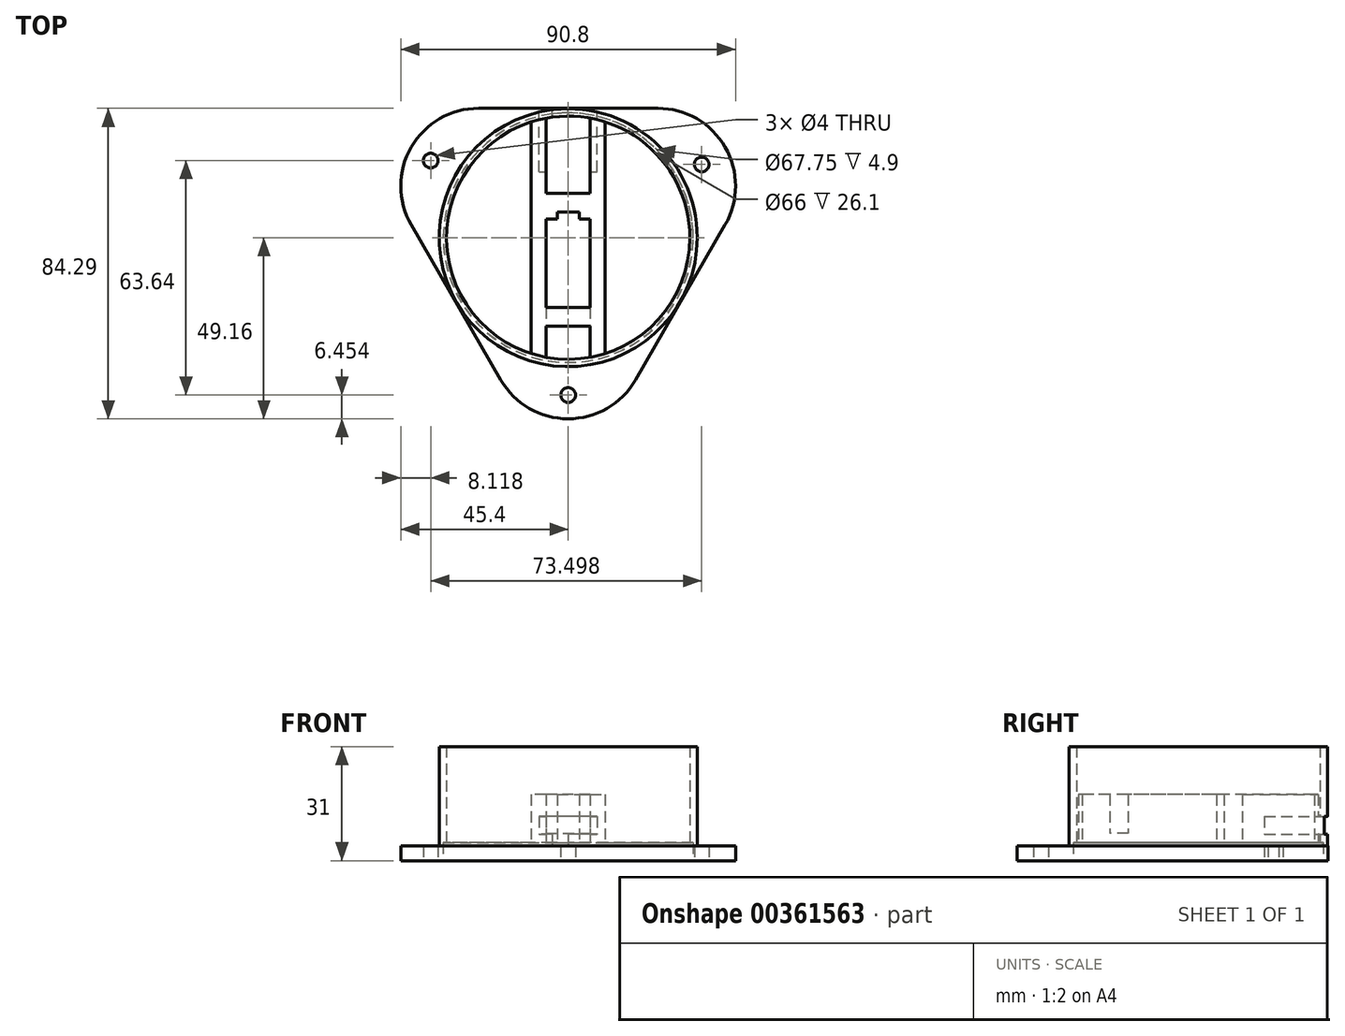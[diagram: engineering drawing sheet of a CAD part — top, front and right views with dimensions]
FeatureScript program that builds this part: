
annotation { "Feature Type Name" : "Feature", "Feature Type Description" : "" }
export const myFeature = defineFeature(function(context is Context, id is Id, definition is map)
    precondition{}
    {
        {
            var Q0;
            Q0=qCreatedBy(makeId("Top.planeOp"),FACE);
            var sketch = newSketch(context, id + "F0", { "sketchPlane" : qUnion([Q0])});
            skCircle(sketch, "E0", {"center": v(0, 0) * mm, "radius": 35 * mm});
            skCircle(sketch, "E1", {"center": v(0, 0) * mm, "radius": 33 * mm});
            skSolve(sketch);
        }
        {
            var Q0;
            Q0=qCreatedBy(makeId("Top.planeOp"),FACE);
            var sketch = newSketch(context, id + "F1", { "sketchPlane" : qUnion([Q0])});
            skPoint(sketch, "E2", {"position": v(0, -24) * mm});
            skPoint(sketch, "E3", {"position": v(0, -19) * mm});
            skPoint(sketch, "E4", {"position": v(6, -19) * mm});
            skPoint(sketch, "E5", {"position": v(-6, -19) * mm});
            skPoint(sketch, "E6", {"position": v(6, -24) * mm});
            skPoint(sketch, "E7", {"position": v(-6, -24) * mm});
            skPoint(sketch, "E8", {"position": v(10, -24) * mm});
            skLineSegment(sketch, "E9", {"start": v(10, -24) * mm, "end": v(10, -32.05) * mm});
            skLineSegment(sketch, "E10", {"start": v(6, -24) * mm, "end": v(6, -33.1) * mm});
            skPoint(sketch, "E11", {"position": v(6, 5) * mm});
            skPoint(sketch, "E12", {"position": v(3, 5) * mm});
            skPoint(sketch, "E13", {"position": v(3, 7) * mm});
            skPoint(sketch, "E14", {"position": v(3, 12) * mm});
            skPoint(sketch, "E15", {"position": v(6, 12) * mm});
            skPoint(sketch, "E16", {"position": v(10, 5) * mm});
            skPoint(sketch, "E17", {"position": v(10, 12) * mm});
            skLineSegment(sketch, "E18", {"start": v(10, -24) * mm, "end": v(10, 32.28) * mm});
            skLineSegment(sketch, "E19", {"start": v(6, 12) * mm, "end": v(6, 33.47) * mm});
            skLineSegment(sketch, "E20", {"start": v(6, 12) * mm, "end": v(3, 12) * mm});
            skLineSegment(sketch, "E21", {"start": v(3, 7) * mm, "end": v(3, 5) * mm});
            skLineSegment(sketch, "E22", {"start": v(3, 5) * mm, "end": v(6, 5) * mm});
            skLineSegment(sketch, "E23", {"start": v(6, 5) * mm, "end": v(6, -19) * mm});
            skPoint(sketch, "E24", {"position": v(0, 7) * mm});
            skPoint(sketch, "E25", {"position": v(0, 12) * mm});
            skLineSegment(sketch, "E26", {"start": v(3, 7) * mm, "end": v(0, 7) * mm});
            skLineSegment(sketch, "E27", {"start": v(3, 12) * mm, "end": v(0, 12) * mm});
            skLineSegment(sketch, "E28", {"start": v(0, -24) * mm, "end": v(6, -24) * mm});
            skLineSegment(sketch, "E29", {"start": v(0, -19) * mm, "end": v(6, -19) * mm});
            skLineSegment(sketch, "E30.MirrorCS", {"start": v(-3, 12) * mm, "end": v(0, 12) * mm});
            skLineSegment(sketch, "E31.MirrorCS", {"start": v(-6, 12) * mm, "end": v(-3, 12) * mm});
            skLineSegment(sketch, "E32.MirrorCS", {"start": v(-6, 12) * mm, "end": v(-6, 33.47) * mm});
            skLineSegment(sketch, "E33.MirrorCS", {"start": v(-10, -24) * mm, "end": v(-10, 32.28) * mm});
            skLineSegment(sketch, "E34.MirrorCS", {"start": v(-6, 5) * mm, "end": v(-6, -19) * mm});
            skLineSegment(sketch, "E35.MirrorCS", {"start": v(-3, 5) * mm, "end": v(-6, 5) * mm});
            skLineSegment(sketch, "E36.MirrorCS", {"start": v(-3, 7) * mm, "end": v(-3, 5) * mm});
            skLineSegment(sketch, "E37.MirrorCS", {"start": v(-3, 7) * mm, "end": v(0, 7) * mm});
            skLineSegment(sketch, "E38.MirrorCS", {"start": v(0, -19) * mm, "end": v(-6, -19) * mm});
            skLineSegment(sketch, "E39.MirrorCS", {"start": v(0, -24) * mm, "end": v(-6, -24) * mm});
            skLineSegment(sketch, "E40.MirrorCS", {"start": v(-6, -24) * mm, "end": v(-6, -33.1) * mm});
            skLineSegment(sketch, "E41.MirrorCS", {"start": v(-10, -24) * mm, "end": v(-10, -32.05) * mm});
            skLineSegment(sketch, "E42", {"start": v(6, 33.47) * mm, "end": v(10, 32.28) * mm});
            skLineSegment(sketch, "E43", {"start": v(-6, 33.47) * mm, "end": v(-10, 32.28) * mm});
            skLineSegment(sketch, "E44", {"start": v(-10, -32.05) * mm, "end": v(-6, -33.1) * mm});
            skLineSegment(sketch, "E45", {"start": v(6, -33.1) * mm, "end": v(10, -32.05) * mm});
            skSolve(sketch);
        }
        {
            var Q0;
            Q0=makeQuery(id+"F0.imprint","IMPRINT",FACE,{"disambiguationData":[TD([[makeQuery(id+"F0.imprint","IMPRINT",EDGE,{"derivedFrom":sQuery(id+"F0.wireOp",EDGE,"E0")}),1.0]])]});
            extrude(context, id + "F2", {"entities" : qUnion([Q0]), "depth" : 31 * mm});
        }
        {
            var Q0;
            Q0=makeQuery(id+"F1.imprint","IMPRINT",FACE,{"disambiguationData":[TD([[makeQuery(id+"F1.imprint","IMPRINT",EDGE,{"derivedFrom":sQuery(id+"F1.wireOp",EDGE,"E9")}),-1.0]])]});
            extrude(context, id + "F3", {"entities" : qUnion([Q0]), "operationType" : NewBodyOperationType.ADD, "depth" : 18 * mm});
        }
        {
            var Q0;
            Q0=sQuery(id+"F1.wireOp",EDGE,"E28");
            var Q1;
            Q1=sQuery(id+"F1.wireOp",EDGE,"E39.MirrorCS");
            extrude(context, id + "F4", {"bodyType" : ToolBodyType.SURFACE, "surfaceEntities" : qUnion([Q0, Q1]), "depth" : 7.5 * mm});
        }
        {
            var Q0;
            Q0=makeQuery(id+"F4.opExtrude","SWEPT_FACE",FACE,{"disambiguationData":[OSD([sQuery(id+"F1.wireOp",EDGE,"E28"),sQuery(id+"F1.wireOp",EDGE,"E39.MirrorCS")])]});
            extrude(context, id + "F5", {"entities" : qUnion([Q0]), "operationType" : NewBodyOperationType.REMOVE, "oppositeDirection" : true, "depth" : 9.3 * mm});
        }
        {
            var Q0;
            Q0=qCreatedBy(makeId("Top.planeOp"),FACE);
            var sketch = newSketch(context, id + "F6", { "sketchPlane" : qUnion([Q0])});
            skCircle(sketch, "E46.cCircle", {"center": v(0, 0) * mm, "radius": 35.13 * mm, "construction": true});
            skLineSegment(sketch, "E46.0", {"start": v(-60.85, 35.13) * mm, "end": v(60.85, 35.13) * mm});
            skLineSegment(sketch, "E46.1", {"start": v(60.85, 35.13) * mm, "end": v(0, -70.26) * mm});
            skLineSegment(sketch, "E46.2", {"start": v(0, -70.26) * mm, "end": v(-60.85, 35.13) * mm});
            skPoint(sketch, "E46.0.midPoint", {"position": v(0, 35.13) * mm});
            skSolve(sketch);
        }
        {
            var Q0;
            Q0=makeQuery(id+"F6.imprint","IMPRINT",FACE,{"disambiguationData":[TD([[makeQuery(id+"F6.imprint","IMPRINT",EDGE,{"derivedFrom":sQuery(id+"F6.wireOp",EDGE,"E46.0")}),-1.0]])]});
            extrude(context, id + "F7", {"entities" : qUnion([Q0]), "operationType" : NewBodyOperationType.ADD, "depth" : 4 * mm});
        }
        {
            var Q0;
            Q0=makeQuery(id+"F7.opExtrude","SWEPT_EDGE",EDGE,{"disambiguationData":[OSD([sQuery(id+"F6.wireOp",EDGE,"E46.0"),sQuery(id+"F6.wireOp",EDGE,"E46.2")])]});
            var Q1;
            Q1=makeQuery(id+"F7.opExtrude","SWEPT_EDGE",EDGE,{"disambiguationData":[OSD([sQuery(id+"F6.wireOp",EDGE,"E46.0"),sQuery(id+"F6.wireOp",EDGE,"E46.1")])]});
            var Q2;
            Q2=makeQuery(id+"F7.opExtrude","SWEPT_EDGE",EDGE,{"disambiguationData":[OSD([sQuery(id+"F6.wireOp",EDGE,"E46.1"),sQuery(id+"F6.wireOp",EDGE,"E46.2")])]});
            fillet(context, id + "F8", {"entities" : qUnion([Q0, Q1, Q2]), "radius" : 21.1 * mm, "tangentPropagation" : true, "allowEdgeOverflow" : false});
        }
        {
            var Q0;
            Q0=qCreatedBy(makeId("Top.planeOp"),FACE);
            var sketch = newSketch(context, id + "F9", { "sketchPlane" : qUnion([Q0])});
            skCircle(sketch, "E47", {"center": v(-37.28, 20.93) * mm, "radius": 2 * mm});
            skCircle(sketch, "E48", {"center": v(0, -42.7) * mm, "radius": 2 * mm});
            skCircle(sketch, "E49", {"center": v(36.22, 19.89) * mm, "radius": 2 * mm});
            skSolve(sketch);
        }
        {
            var Q0;
            Q0 = qSketchRegion(id + "F9", true);
            extrude(context, id + "F10", {"entities" : qUnion([Q0]), "operationType" : NewBodyOperationType.REMOVE, "oppositeDirection" : true, "depth" : 38 * mm});
        }
        {
            var Q0;
            Q0=makeQuery(id+"F9.imprint","IMPRINT",FACE,{"disambiguationData":[TD([[makeQuery(id+"F9.imprint","IMPRINT",EDGE,{"derivedFrom":sQuery(id+"F9.wireOp",EDGE,"E49")}),1.0]])]});
            extrude(context, id + "F11", {"entities" : qUnion([Q0]), "operationType" : NewBodyOperationType.REMOVE, "depth" : 52 * mm});
        }
        {
            var Q0;
            Q0=makeQuery(id+"F9.imprint","IMPRINT",FACE,{"disambiguationData":[TD([[makeQuery(id+"F9.imprint","IMPRINT",EDGE,{"derivedFrom":sQuery(id+"F9.wireOp",EDGE,"E47")}),1.0]])]});
            var Q1;
            Q1=makeQuery(id+"F9.imprint","IMPRINT",FACE,{"disambiguationData":[TD([[makeQuery(id+"F9.imprint","IMPRINT",EDGE,{"derivedFrom":sQuery(id+"F9.wireOp",EDGE,"E48")}),1.0]])]});
            extrude(context, id + "F12", {"entities" : qUnion([Q0, Q1]), "operationType" : NewBodyOperationType.REMOVE, "depth" : 37.9 * mm});
        }
        {
            var Q0;
            Q0=qCreatedBy(makeId("Top.planeOp"),FACE);
            var sketch = newSketch(context, id + "F13", { "sketchPlane" : qUnion([Q0])});
            skCircle(sketch, "E50", {"center": v(0, 0) * mm, "radius": 33.88 * mm});
            skSolve(sketch);
        }
        {
            var Q0;
            Q0 = qSketchRegion(id + "F13", true);
            extrude(context, id + "F14", {"entities" : qUnion([Q0]), "operationType" : NewBodyOperationType.REMOVE, "depth" : 4.9 * mm});
        }
        {
            var Q0;
            Q0=makeQuery(id+"F7.opExtrude","SWEPT_FACE",FACE,{"disambiguationData":[OSD([sQuery(id+"F6.wireOp",EDGE,"E46.0")])]});
            var sketch = newSketch(context, id + "F15", { "sketchPlane" : qUnion([Q0])});
            skLineSegment(sketch, "E51", {"start": v(-2.22, 1.63) * mm, "end": v(0, 9.6) * mm});
            skLineSegment(sketch, "E52.bottom", {"start": v(7.87, 12) * mm, "end": v(-7.87, 12) * mm});
            skLineSegment(sketch, "E52.top", {"start": v(7.87, 7.19) * mm, "end": v(-7.87, 7.19) * mm});
            skLineSegment(sketch, "E52.left", {"start": v(7.87, 12) * mm, "end": v(7.87, 7.19) * mm});
            skLineSegment(sketch, "E52.right", {"start": v(-7.87, 12) * mm, "end": v(-7.87, 7.19) * mm});
            skPoint(sketch, "E52.middle", {"position": v(0, 9.6) * mm});
            skLineSegment(sketch, "E53.bottom", {"start": v(4.3, 4) * mm, "end": v(0, 4) * mm});
            skLineSegment(sketch, "E53.top", {"start": v(4.3, 10.38) * mm, "end": v(0, 10.38) * mm});
            skLineSegment(sketch, "E53.left", {"start": v(4.3, 4) * mm, "end": v(4.3, 10.38) * mm});
            skLineSegment(sketch, "E53.right", {"start": v(0, 4) * mm, "end": v(0, 10.38) * mm});
            skPoint(sketch, "E53.middle", {"position": v(2.15, 7.19) * mm});
            skSolve(sketch);
        }
        {
            var Q0;
            Q0=makeQuery(id+"F15.imprint","IMPRINT",FACE,{"disambiguationData":[TD([[makeQuery(id+"F15.imprint","IMPRINT",EDGE,{"derivedFrom":sQuery(id+"F15.wireOp",EDGE,"E52.bottom")}),1.0]])]});
            var Q1;
            {var subQ5=sQuery(id+"F15.wireOp",EDGE,"E53.top");Q1=makeQuery(id+"F15.imprint","IMPRINT",FACE,{"disambiguationData":[TD([[makeQuery(id+"F15.imprint","IMPRINT",EDGE,{"derivedFrom":subQ5}),1.0]])]});}
            var Q2;
            {var subQ5=sQuery(id+"F15.wireOp",EDGE,"E53.bottom");Q2=makeQuery(id+"F15.imprint","IMPRINT",FACE,{"disambiguationData":[TD([[makeQuery(id+"F15.imprint","IMPRINT",EDGE,{"derivedFrom":subQ5}),-1.0]])]});}
            extrude(context, id + "F16", {"entities" : qUnion([Q0, Q1, Q2]), "operationType" : NewBodyOperationType.REMOVE, "oppositeDirection" : true, "depth" : 17.2 * mm});
        }
    });
